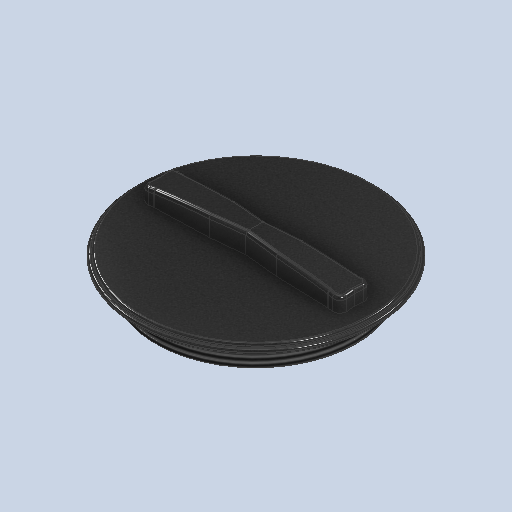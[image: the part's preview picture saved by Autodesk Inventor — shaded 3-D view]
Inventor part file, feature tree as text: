
AUTODESK INVENTOR PART (.ipt)
format: ipt  version: 2024.2 (Build 282272000, 272)  size: 784,896 bytes
history: native  units: mm
features: sketch x8, extrude x7, fillet x3, projected_geometry x2, other x1, thread x1, shell x1
ambient origin geometry x8: Origin, YZ Plane, XZ Plane, XY Plane, X Axis, Y Axis, Z Axis, Center Point
bodies: Body1 (feature_tree)
feature tree (23):
  other  "Твердое тело1"
  extrude  "Выдавливание1"  Depth=300.0mm
  extrude  "Выдавливание2"  Depth=38.0mm TaperAngle=0.0deg
  extrude  "Выдавливание3"  Depth=358.0mm
  extrude  "Выдавливание4"  Depth=40.0mm TaperAngle=0.0deg
  extrude  "Выдавливание5"  Depth=5.0mm
  extrude  "Выдавливание6"  Depth=35.0mm TaperAngle=0.0deg
  extrude  "Выдавливание7"  Depth=5.0mm
  sketch  "Эскиз13"
  fillet  "Сопряжение1"  Radius=5.0mm
  fillet  "Сопряжение2"  Radius=30.0mm
  thread  "Резьба1"
  fillet  "Сопряжение3"  Radius=300.0mm
  shell  "Оболочка1"  Thickness=50.0mm
  sketch  "Эскиз1"
  sketch  "Эскиз2"
  sketch  "Эскиз3"
  projected_geometry  "Спроецированная петля1"
  sketch  "Эскиз5"
  sketch  "Эскиз6"
  sketch  "Эскиз7"
  projected_geometry  "Спроецированная петля2"
  sketch  "Эскиз8"
